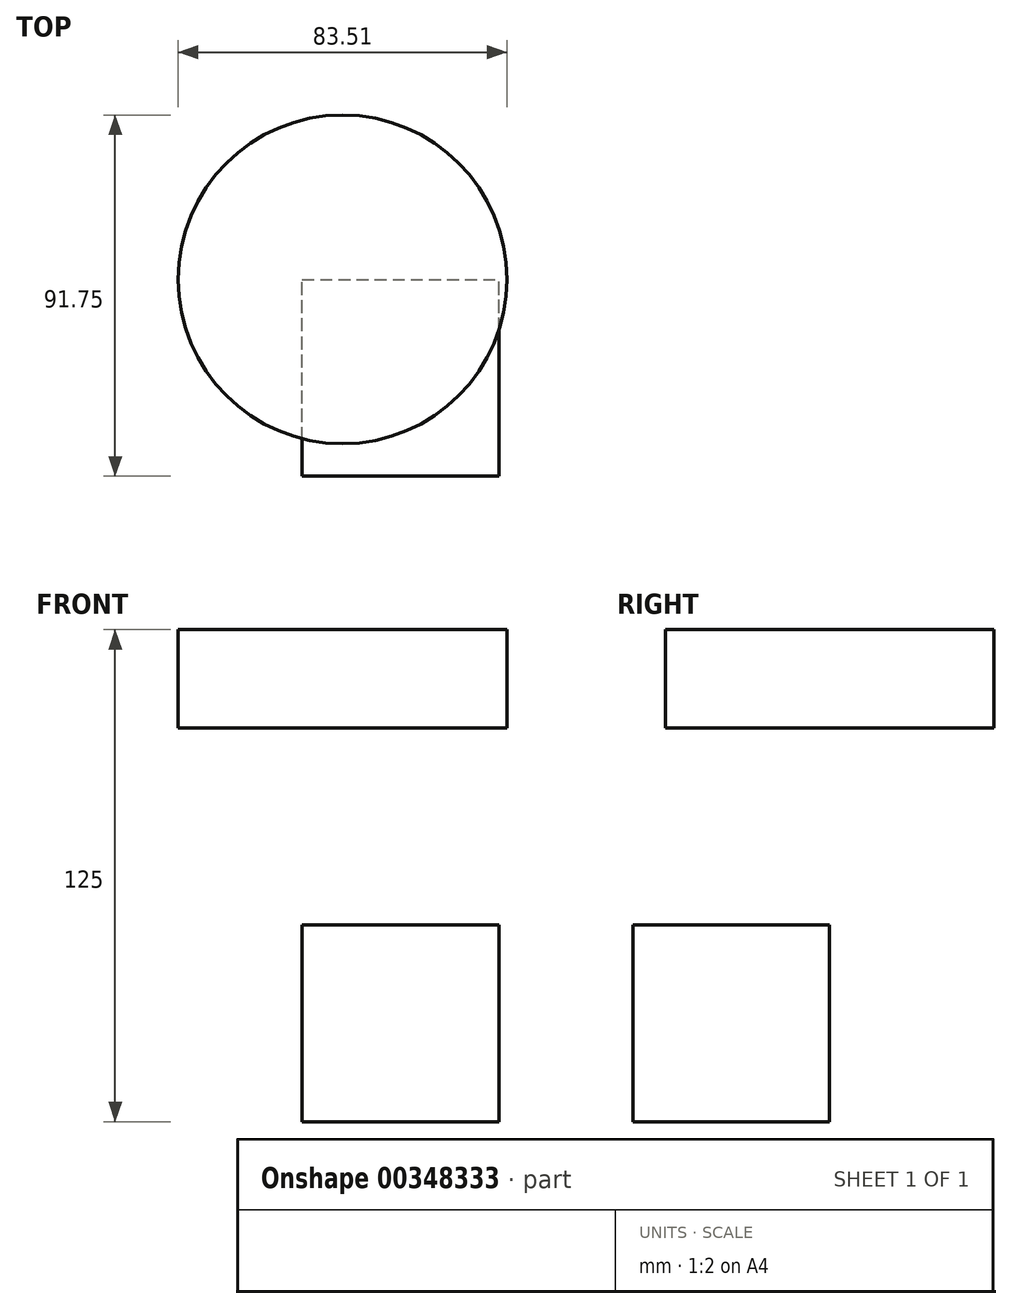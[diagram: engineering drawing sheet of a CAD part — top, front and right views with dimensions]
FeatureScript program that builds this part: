
annotation { "Feature Type Name" : "Feature", "Feature Type Description" : "" }
export const myFeature = defineFeature(function(context is Context, id is Id, definition is map)
    precondition{}
    {
        {
            var Q0;
            Q0=qCreatedBy(makeId("Front.planeOp"),FACE);
            var sketch = newSketch(context, id + "F0", { "sketchPlane" : qUnion([Q0])});
            skLineSegment(sketch, "E0.bottom", {"start": v(0, 0) * mm, "end": v(50, 0) * mm});
            skLineSegment(sketch, "E0.top", {"start": v(0, 50) * mm, "end": v(50, 50) * mm});
            skLineSegment(sketch, "E0.left", {"start": v(0, 0) * mm, "end": v(0, 50) * mm});
            skLineSegment(sketch, "E0.right", {"start": v(50, 0) * mm, "end": v(50, 50) * mm});
            skSolve(sketch);
        }
        {
            var Q0;
            Q0 = qSketchRegion(id + "F0", true);
            extrude(context, id + "F1", {"entities" : qUnion([Q0]), "depth" : 50 * mm});
        }
        {
            var Q0;
            Q0=qCreatedBy(makeId("Top.planeOp"),FACE);
            cPlane(context, id + "F2", {"entities" : qUnion([Q0]), "cplaneType" : CPlaneType.OFFSET, "offset" : 100 * mm, "width" : 150 * mm, "height" : 150 * mm});
        }
        {
            var Q0;
            Q0=qCreatedBy(id+"F2.planeOp",FACE);
            var sketch = newSketch(context, id + "F3", { "sketchPlane" : qUnion([Q0])});
            skCircle(sketch, "E1", {"center": v(10.23, 0) * mm, "radius": 41.75 * mm});
            skSolve(sketch);
        }
        {
            var Q0;
            Q0 = qSketchRegion(id + "F3", true);
            extrude(context, id + "F4", {"entities" : qUnion([Q0]), "depth" : 25 * mm});
        }
    });
